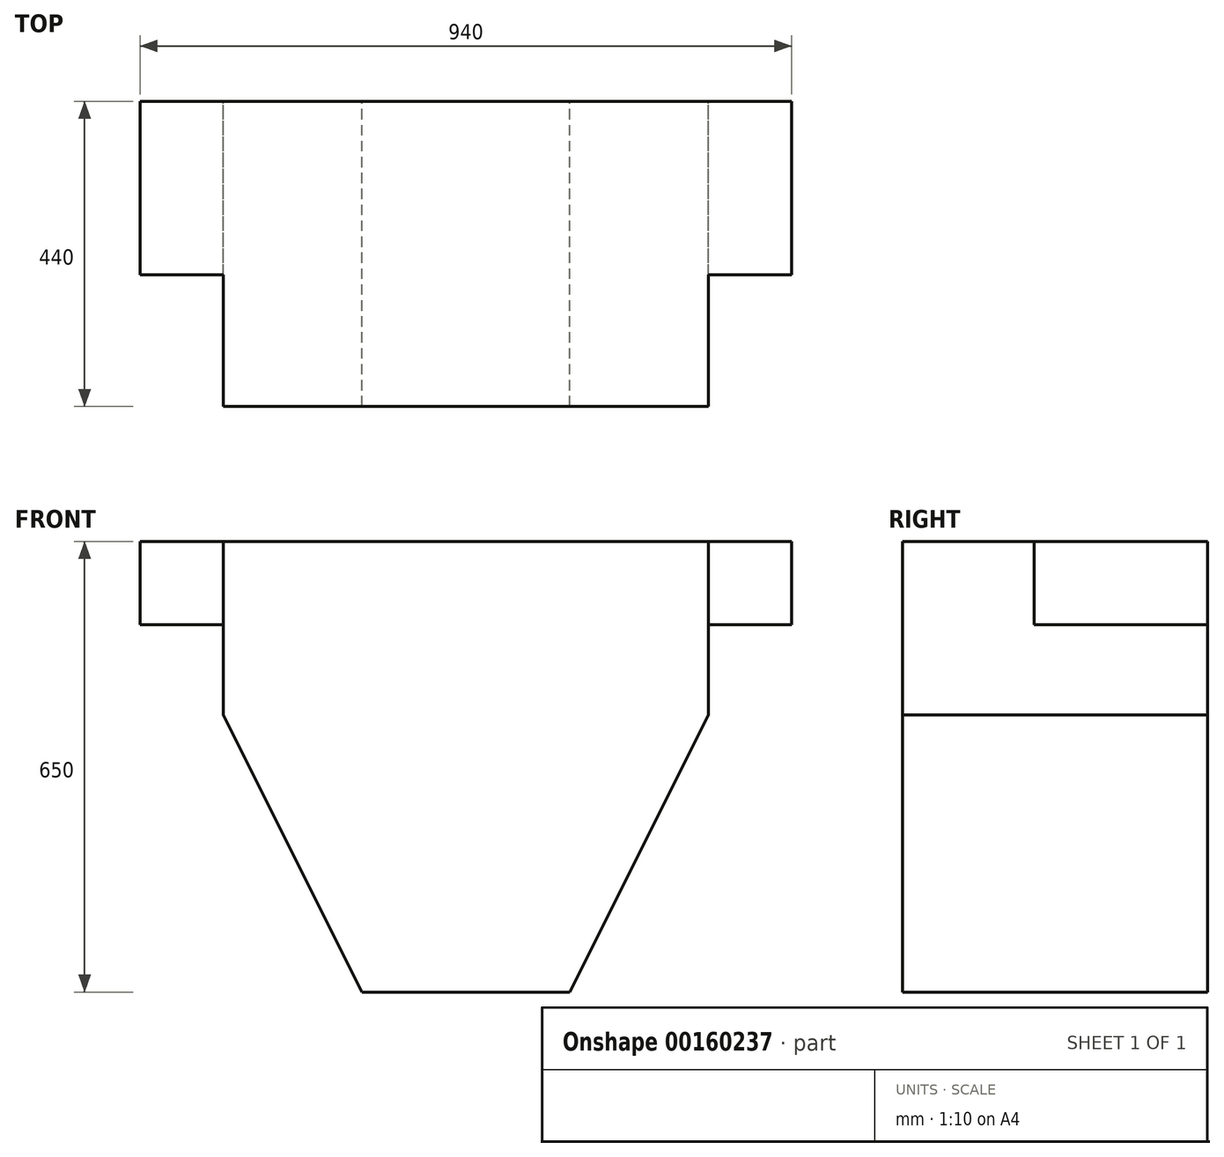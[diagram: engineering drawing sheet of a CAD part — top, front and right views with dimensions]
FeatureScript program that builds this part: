
annotation { "Feature Type Name" : "Feature", "Feature Type Description" : "" }
export const myFeature = defineFeature(function(context is Context, id is Id, definition is map)
    precondition{}
    {
        {
            var Q0;
            Q0=qCreatedBy(makeId("Front.planeOp"),FACE);
            var sketch = newSketch(context, id + "F0", { "sketchPlane" : qUnion([Q0])});
            skLineSegment(sketch, "E0.bottom", {"start": v(150, -325) * mm, "end": v(-150, -325) * mm});
            skLineSegment(sketch, "E0.top", {"start": v(350, 325) * mm, "end": v(-350, 325) * mm});
            skLineSegment(sketch, "E0.left", {"start": v(350, 75) * mm, "end": v(350, 325) * mm});
            skLineSegment(sketch, "E0.right", {"start": v(-350, 75) * mm, "end": v(-350, 325) * mm});
            skPoint(sketch, "E0.middle", {"position": v(0, 0) * mm});
            skLineSegment(sketch, "E1", {"start": v(-150, -325) * mm, "end": v(-350, 75) * mm});
            skLineSegment(sketch, "E2", {"start": v(150, -325) * mm, "end": v(350, 75) * mm});
            skPoint(sketch, "E3.orphan", {"position": v(350, -325) * mm});
            skPoint(sketch, "E4.orphan", {"position": v(-350, -325) * mm});
            skSolve(sketch);
        }
        {
            var Q0;
            Q0 = qSketchRegion(id + "F0", true);
            extrude(context, id + "F1", {"entities" : qUnion([Q0]), "depth" : 440 * mm});
        }
        {
            var Q0;
            Q0=makeQuery(id+"F1.opExtrude","SWEPT_FACE",FACE,{"disambiguationData":[OSD([sQuery(id+"F0.wireOp",EDGE,"E0.top")])]});
            var sketch = newSketch(context, id + "F2", { "sketchPlane" : qUnion([Q0])});
            skLineSegment(sketch, "E5.bottom", {"start": v(350, 0) * mm, "end": v(470, 0) * mm});
            skLineSegment(sketch, "E5.top", {"start": v(350, -250) * mm, "end": v(470, -250) * mm});
            skLineSegment(sketch, "E5.left", {"start": v(350, 0) * mm, "end": v(350, -250) * mm});
            skLineSegment(sketch, "E5.right", {"start": v(470, 0) * mm, "end": v(470, -250) * mm});
            skLineSegment(sketch, "E6.bottom", {"start": v(-350, 0) * mm, "end": v(-470, 0) * mm});
            skLineSegment(sketch, "E6.top", {"start": v(-350, -250) * mm, "end": v(-470, -250) * mm});
            skLineSegment(sketch, "E6.left", {"start": v(-350, 0) * mm, "end": v(-350, -250) * mm});
            skLineSegment(sketch, "E6.right", {"start": v(-470, 0) * mm, "end": v(-470, -250) * mm});
            skSolve(sketch);
        }
        {
            var Q0;
            Q0 = qSketchRegion(id + "F2", true);
            extrude(context, id + "F3", {"entities" : qUnion([Q0]), "operationType" : NewBodyOperationType.ADD, "oppositeDirection" : true, "depth" : 120 * mm});
        }
    });
